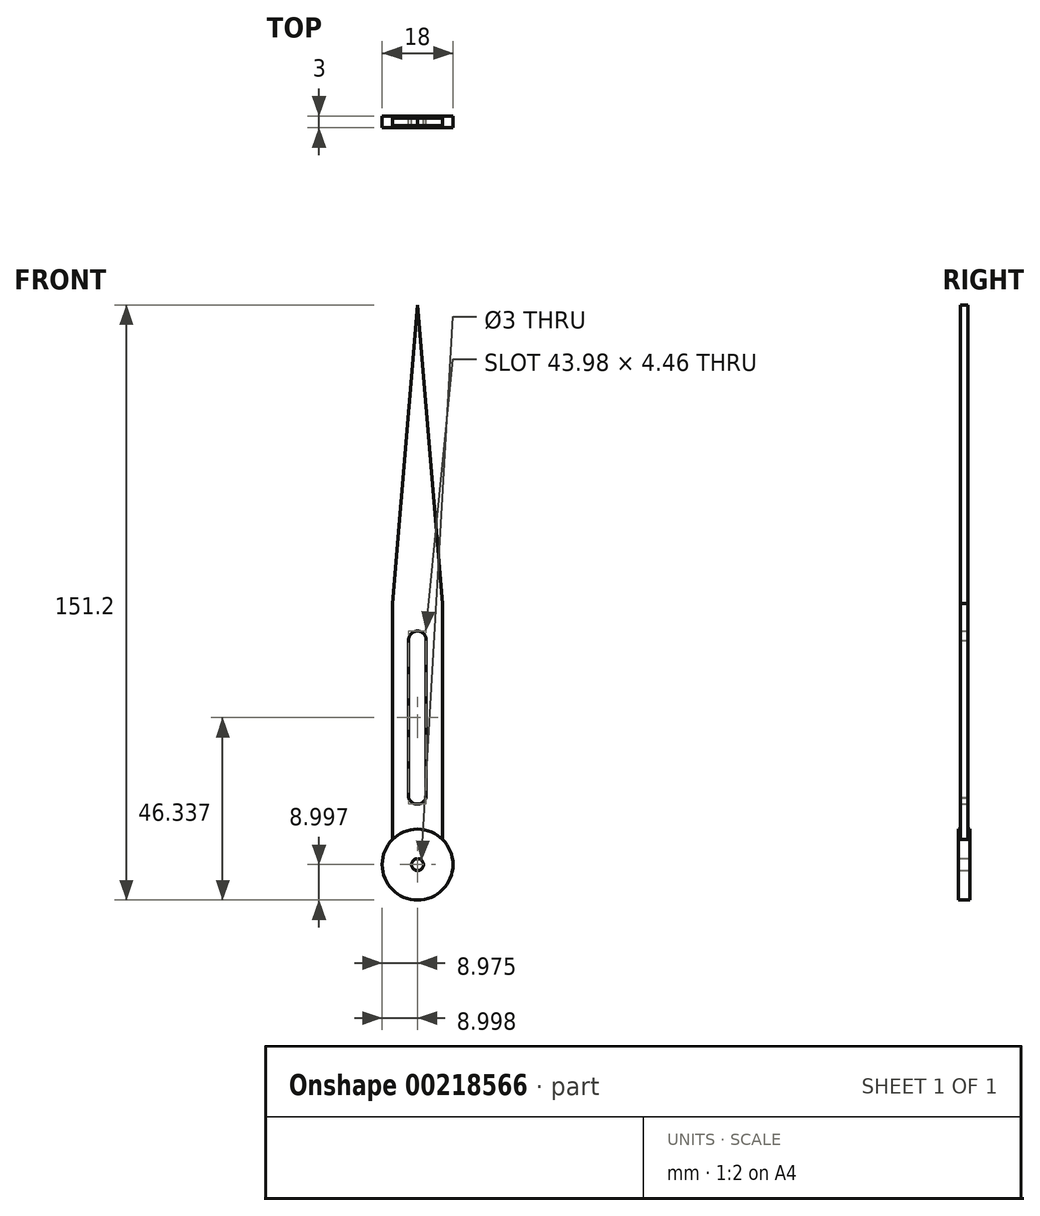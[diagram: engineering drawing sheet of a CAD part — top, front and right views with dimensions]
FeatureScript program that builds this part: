
annotation { "Feature Type Name" : "Feature", "Feature Type Description" : "" }
export const myFeature = defineFeature(function(context is Context, id is Id, definition is map)
    precondition{}
    {
        {
            var Q0;
            Q0=qCreatedBy(makeId("Front.planeOp"),FACE);
            var sketch = newSketch(context, id + "F0", { "sketchPlane" : qUnion([Q0])});
            skCircle(sketch, "E0", {"center": v(-20.04, -44.31) * mm, "radius": 1.5 * mm});
            skCircle(sketch, "E1", {"center": v(-20.04, -44.31) * mm, "radius": 9 * mm});
            skLineSegment(sketch, "E2.left", {"start": v(-26.41, -37.96) * mm, "end": v(-26.41, 22.04) * mm});
            skLineSegment(sketch, "E3", {"start": v(-26.41, 22.04) * mm, "end": v(-20.04, 97.89) * mm});
            skArc(sketch, "E4", {"start": v(-22.3, -27.34) * mm, "mid": v(-20.02, -28.97) * mm, "end": v(-17.83, -27.21) * mm});
            skArc(sketch, "E5", {"start": v(-17.83, 12.79) * mm, "mid": v(-20.13, 15.02) * mm, "end": v(-22.3, 12.66) * mm});
            skLineSegment(sketch, "E6.MirrorCS", {"start": v(-22.3, 12.66) * mm, "end": v(-22.3, -27.34) * mm});
            skLineSegment(sketch, "E7.MirrorCS", {"start": v(-13.67, 22.04) * mm, "end": v(-20.04, 97.89) * mm});
            skLineSegment(sketch, "E8.MirrorCS", {"start": v(-13.67, -37.96) * mm, "end": v(-13.67, 22.04) * mm});
            skLineSegment(sketch, "E9.MirrorCS", {"start": v(-17.83, 12.79) * mm, "end": v(-17.83, -27.21) * mm});
            skSolve(sketch);
        }
        {
            var Q0;
            Q0=makeQuery(id+"F0.imprint","IMPRINT",FACE,{"disambiguationData":[TD([[makeQuery(id+"F0.imprint","IMPRINT",EDGE,{"derivedFrom":sQuery(id+"F0.wireOp",EDGE,"E0")}),-1.0]])]});
            var Q1;
            Q1=sQuery(id+"F0.wireOp",EDGE,"p5VHldXC-XaDy-Jo6Q-gzRM-BKwmdG1nrnMR");
            var Q2;
            Q2=sQuery(id+"F0.wireOp",EDGE,"WyDkhZpA-9s04-8oUv-ohR5-d8g4u36zodpv");
            var Q3;
            Q3=sQuery(id+"F0.wireOp",EDGE,"zPygVgP6-IXea-uzZJ-7nVa-Sz4MqIU0xlYZ");
            extrude(context, id + "F1", {"entities" : qUnion([Q0]), "surfaceEntities" : qUnion([Q1, Q2, Q3]), "depth" : 3 * mm, "symmetric" : true});
        }
        {
            var Q0;
            Q0=makeQuery(id+"F0.imprint","IMPRINT",FACE,{"disambiguationData":[TD([[makeQuery(id+"F0.imprint","IMPRINT",EDGE,{"derivedFrom":sQuery(id+"F0.wireOp",EDGE,"64VVkBTR-3lK9-xNKO-ebiv-tDq6J559YHrB.left")}),-1.0]])]});
            var Q1;
            {var subQ4=sQuery(id+"F0.wireOp",EDGE,"E2.left");Q1=makeQuery(id+"F0.imprint","IMPRINT",FACE,{"disambiguationData":[TD([[makeQuery(id+"F0.imprint","IMPRINT",EDGE,{"derivedFrom":subQ4}),-1.0]])]});}
            extrude(context, id + "F2", {"entities" : qUnion([Q0, Q1]), "operationType" : NewBodyOperationType.ADD, "depth" : 2 * mm, "symmetric" : true});
        }
    });
